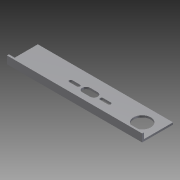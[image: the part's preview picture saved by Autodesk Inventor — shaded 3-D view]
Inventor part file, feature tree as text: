
AUTODESK INVENTOR PART (.ipt)
format: ipt  version: 2012 (Build 160160000, 160)  size: 103,424 bytes
history: native  units: in
note: dims shown in document units (in); Inventor stores cm internally (conversion verified against a paired STEP export)
features: other x3, sketch x2, extrude x1
ambient origin geometry x8: Origin, YZ Plane, XZ Plane, XY Plane, X Axis, Y Axis, Z Axis, Center Point
bodies: Solid1 (feature_tree)
feature tree (6):
  other  "8 ball bottom 1 by 2 L short.ipt"
  extrude  "Extrusion1"  Depth=0.1in
  other  "Solid1::8 ball bottom 1 by 2 L short.ipt"
  sketch  "Sketch1"  dims[d0=0.3937in d1=0.1in]
  sketch  "Sketch2"  dims[d2=0.5in d3=0.25in d4=0.5in d5=1.0in d6=2.125in d7=0.7874in d9=2.0in d10=0.3937in d12=1.0in d14=1.0in d15=0.0in]
  other  "TaggingFeature1"
